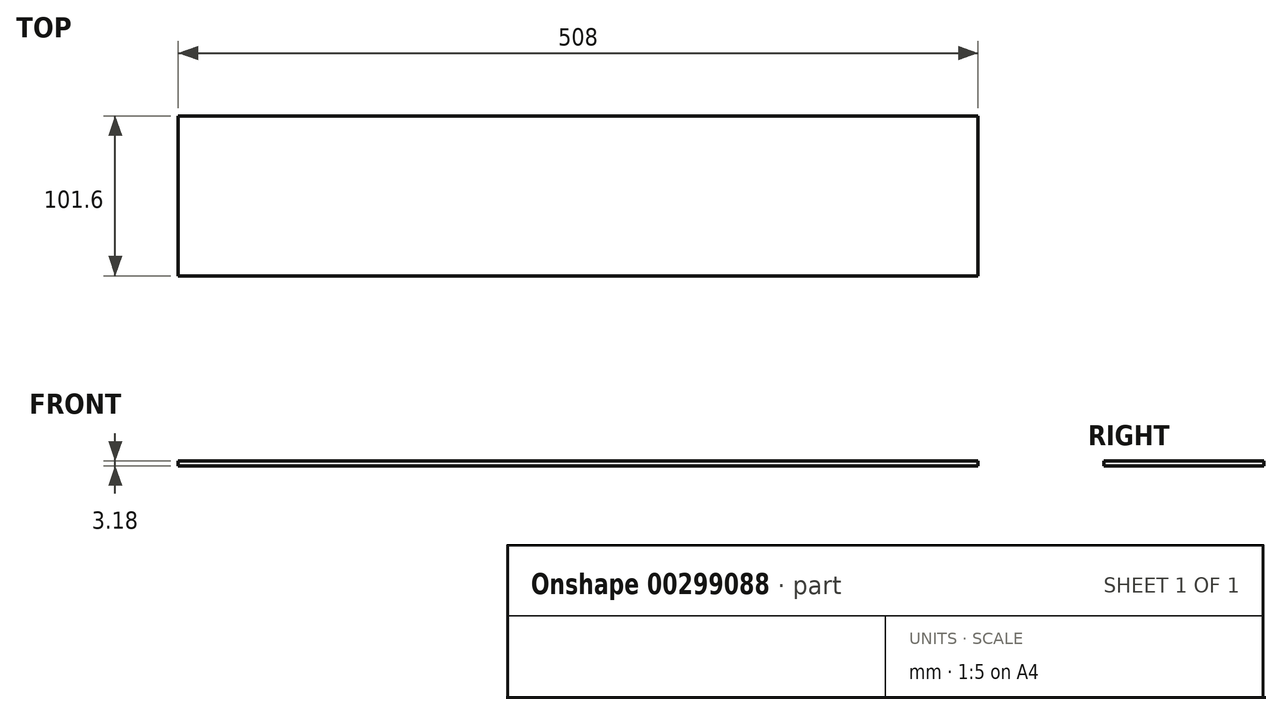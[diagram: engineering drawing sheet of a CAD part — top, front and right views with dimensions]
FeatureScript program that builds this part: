
annotation { "Feature Type Name" : "Feature", "Feature Type Description" : "" }
export const myFeature = defineFeature(function(context is Context, id is Id, definition is map)
    precondition{}
    {
        {
            var Q0;
            Q0=qCreatedBy(makeId("Top.planeOp"),FACE);
            var sketch = newSketch(context, id + "F0", { "sketchPlane" : qUnion([Q0])});
            skLineSegment(sketch, "E0.bottom", {"start": v(-254, -50.8) * mm, "end": v(254, -50.8) * mm});
            skLineSegment(sketch, "E0.top", {"start": v(-254, 50.8) * mm, "end": v(254, 50.8) * mm});
            skLineSegment(sketch, "E0.left", {"start": v(-254, -50.8) * mm, "end": v(-254, 50.8) * mm});
            skLineSegment(sketch, "E0.right", {"start": v(254, -50.8) * mm, "end": v(254, 50.8) * mm});
            skPoint(sketch, "E0.middle", {"position": v(0, 0) * mm});
            skSolve(sketch);
        }
        {
            var Q0;
            Q0 = qSketchRegion(id + "F0", true);
            extrude(context, id + "F1", {"entities" : qUnion([Q0]), "endBound" : BoundingType.SYMMETRIC, "depth" : 3.17 * mm});
        }
    });
